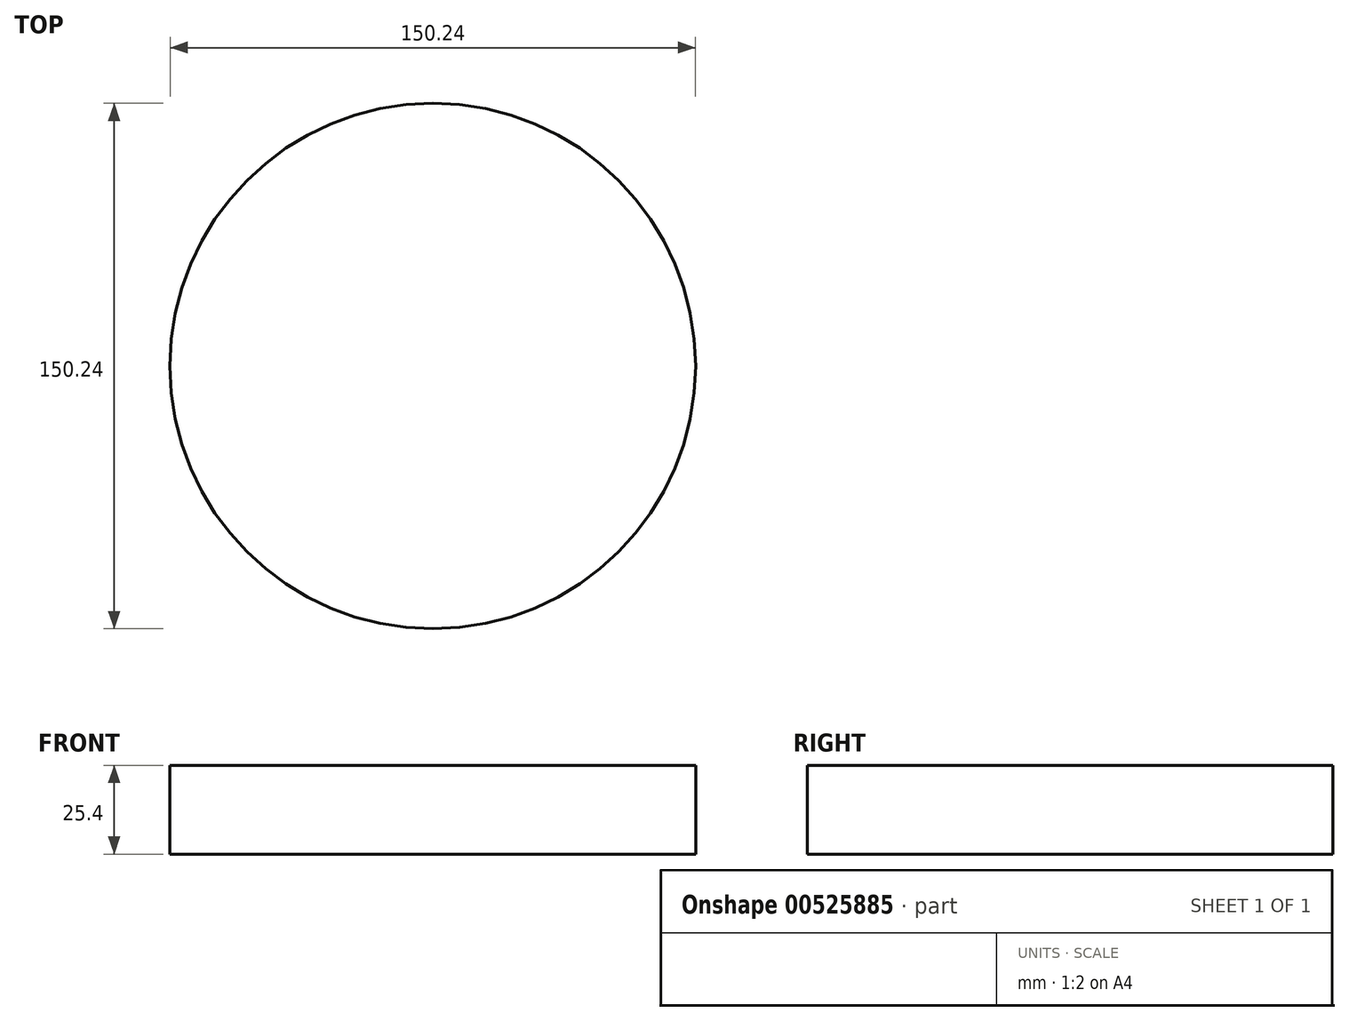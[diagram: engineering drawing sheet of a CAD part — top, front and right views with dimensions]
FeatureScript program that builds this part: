
annotation { "Feature Type Name" : "Feature", "Feature Type Description" : "" }
export const myFeature = defineFeature(function(context is Context, id is Id, definition is map)
    precondition{}
    {
        {
            var Q0;
            Q0=qCreatedBy(makeId("Top.planeOp"),FACE);
            var sketch = newSketch(context, id + "F0", { "sketchPlane" : qUnion([Q0])});
            skCircle(sketch, "E0", {"center": v(0, 0) * mm, "radius": 75.12 * mm});
            skSolve(sketch);
        }
        {
            var Q0;
            Q0 = qSketchRegion(id + "F0", true);
            extrude(context, id + "F1", {"entities" : qUnion([Q0]), "depth" : 25.4 * mm, "offsetDistance" : 25.4 * mm});
        }
    });
